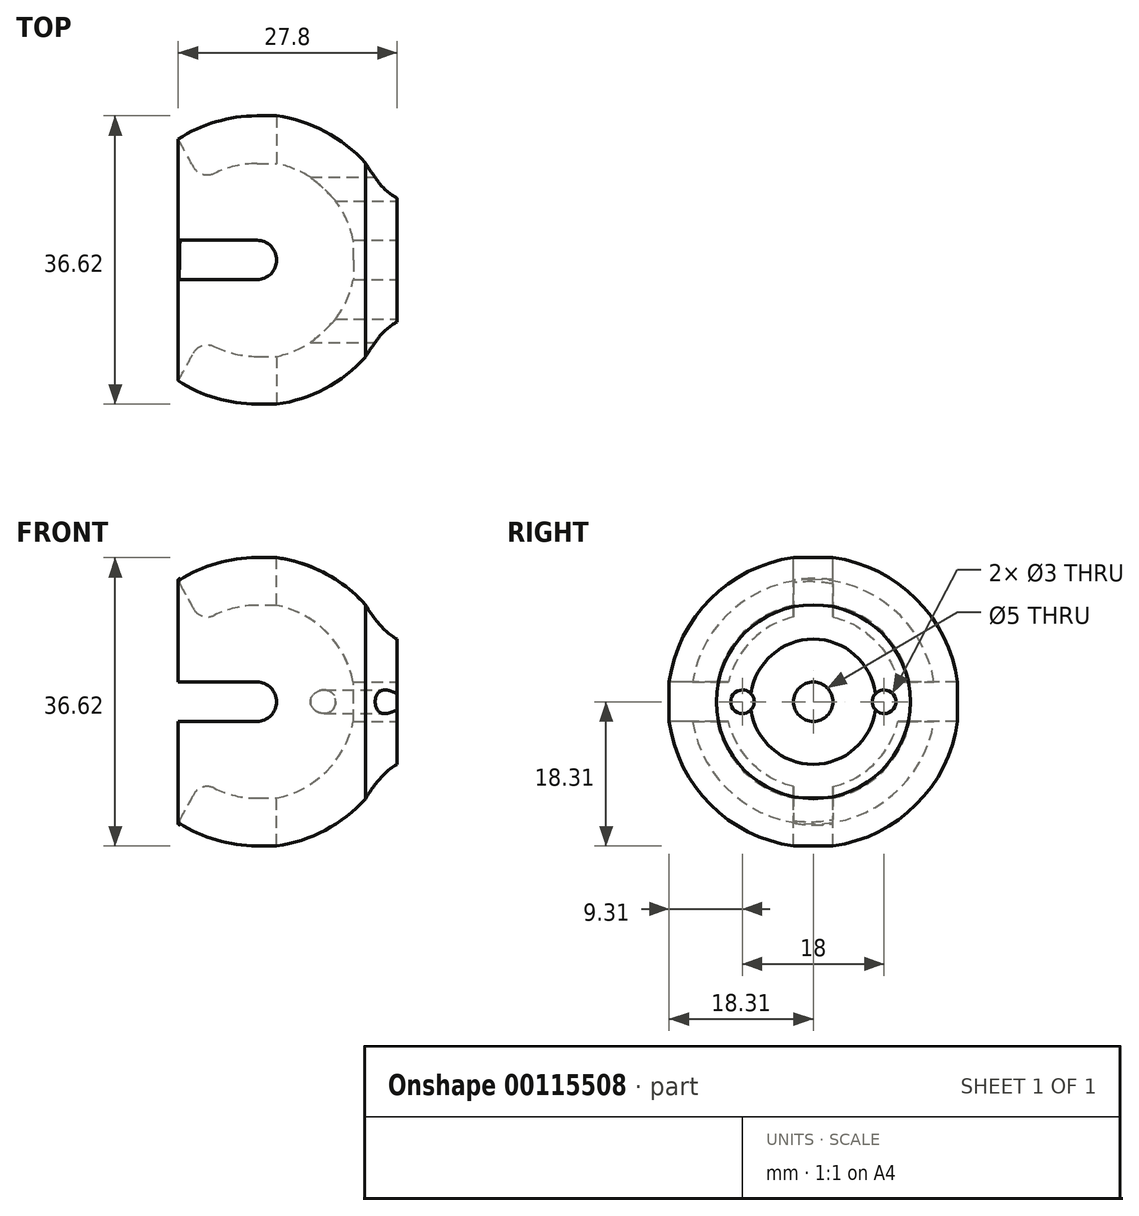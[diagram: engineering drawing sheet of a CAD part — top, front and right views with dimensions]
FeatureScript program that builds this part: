
annotation { "Feature Type Name" : "Feature", "Feature Type Description" : "" }
export const myFeature = defineFeature(function(context is Context, id is Id, definition is map)
    precondition{}
    {
        {
            var Q0;
            Q0=qCreatedBy(makeId("Front.planeOp"),FACE);
            var sketch = newSketch(context, id + "F0", { "sketchPlane" : qUnion([Q0])});
            skLineSegment(sketch, "E0", {"start": v(12.5, 0) * mm, "end": v(57.5, 0) * mm});
            skArc(sketch, "E1", {"start": v(12.46, 0.95) * mm, "mid": v(5.4, 11.27) * mm, "end": v(-7.07, 10.3) * mm});
            skFitSpline(sketch, "E2", {"points": [v(13.78, 12.32) * mm, v(24.8, 6.77) * mm, v(61.3, 8.08) * mm], "startDerivative": vector(27.08, -44.66) * mm, "endDerivative": vector(62.99, 8.12) * mm});
            skLineSegment(sketch, "E3", {"start": v(12.46, 0.95) * mm, "end": v(17.8, 0.95) * mm});
            skPoint(sketch, "E4.end.orphan", {"position": v(82.25, 0.95) * mm});
            skPoint(sketch, "E5.orphan", {"position": v(82.5, -1.55) * mm});
            skArc(sketch, "E6", {"start": v(13.78, 12.32) * mm, "mid": v(2.48, 18.32) * mm, "end": v(-10, 15.54) * mm});
            skLineSegment(sketch, "E7", {"start": v(-7.07, 10.3) * mm, "end": v(-10, 15.54) * mm});
            skLineSegment(sketch, "E8", {"start": v(17.8, 7.95) * mm, "end": v(17.8, 0.95) * mm});
            skPoint(sketch, "E9.start.orphan", {"position": v(74.25, 0.95) * mm});
            skSolve(sketch);
        }
        {
            var Q0;
            Q0=makeQuery(id+"F0.imprint","IMPRINT",FACE,{"disambiguationData":[TD([[makeQuery(id+"F0.imprint","IMPRINT",EDGE,{"derivedFrom":sQuery(id+"F0.wireOp",EDGE,"E1")}),-1.0]])]});
            var Q1;
            Q1=sQuery(id+"F0.wireOp",EDGE,"E0");
            revolve(context, id + "F1", {"entities" : qUnion([Q0]), "axis" : qUnion([Q1]), "revolveType" : RevolveType.FULL});
        }
        {
            var Q0;
            Q0=makeQuery(id+"F1.opRevolve","SWEPT_EDGE",EDGE,{"disambiguationData":[OSD([sQuery(id+"F0.wireOp",EDGE,"E1"),sQuery(id+"F0.wireOp",EDGE,"CbFEBDJi-CplH-pibZ-NPAv-z09MQRNn6UNR")])]});
            var Q1;
            Q1=makeQuery(id+"F1.opRevolve","SWEPT_EDGE",EDGE,{"disambiguationData":[OSD([sQuery(id+"F0.wireOp",EDGE,"E9"),sQuery(id+"F0.wireOp",EDGE,"8ef04d3b-c97b-4cb2-96d4-a3e5af4470d5.trimOffspring")])]});
            fillet(context, id + "F2", {"entities" : qUnion([Q0, Q1]), "radius" : 2 * mm, "tangentPropagation" : true, "allowEdgeOverflow" : false});
        }
        {
            var Q0;
            Q0=makeQuery(id+"F1.opRevolve","SWEPT_FACE",FACE,{"disambiguationData":[OSD([sQuery(id+"F0.wireOp",EDGE,"E8")])]});
            var sketch = newSketch(context, id + "F3", { "sketchPlane" : qUnion([Q0])});
            skCircle(sketch, "E10", {"center": v(-9, 0) * mm, "radius": 1.5 * mm});
            skCircle(sketch, "E11", {"center": v(9, 0) * mm, "radius": 1.5 * mm});
            skCircle(sketch, "E12", {"center": v(0, 0) * mm, "radius": 2.5 * mm});
            skSolve(sketch);
        }
        {
            var Q0;
            {var subQ0=sQuery(id+"F3.wireOp",EDGE,"E10");var subQ1=makeQuery(id+"F1.opRevolve","SWEPT_EDGE",EDGE,{"disambiguationData":[OSD([sQuery(id+"F0.wireOp",EDGE,"E2"),sQuery(id+"F0.wireOp",EDGE,"E8")])]});var subQ2=makeQuery(id+"F3.imprint","INTERSECT",VERTEX,{"disambiguationData":[OD(0.0)],"derivedFrom":[subQ1,subQ0]});Q0=makeQuery(id+"F3.imprint","IMPRINT",FACE,{"disambiguationData":[TD([[makeQuery(id+"F3.imprint","IMPRINT",EDGE,{"disambiguationData":[TD([[subQ2,-1.0]])],"derivedFrom":subQ0}),1.0]])]});}
            var Q1;
            {var subQ0=sQuery(id+"F3.wireOp",EDGE,"E11");var subQ1=makeQuery(id+"F1.opRevolve","SWEPT_EDGE",EDGE,{"disambiguationData":[OSD([sQuery(id+"F0.wireOp",EDGE,"E2"),sQuery(id+"F0.wireOp",EDGE,"E8")])]});var subQ2=makeQuery(id+"F3.imprint","INTERSECT",VERTEX,{"disambiguationData":[OD(0.0)],"derivedFrom":[subQ1,subQ0]});Q1=makeQuery(id+"F3.imprint","IMPRINT",FACE,{"disambiguationData":[TD([[makeQuery(id+"F3.imprint","IMPRINT",EDGE,{"disambiguationData":[TD([[subQ2,-1.0]])],"derivedFrom":subQ0}),1.0]])]});}
            var Q2;
            {var subQ0=sQuery(id+"F3.wireOp",EDGE,"E11");var subQ1=makeQuery(id+"F1.opRevolve","SWEPT_EDGE",EDGE,{"disambiguationData":[OSD([sQuery(id+"F0.wireOp",EDGE,"E2"),sQuery(id+"F0.wireOp",EDGE,"E8")])]});var subQ2=makeQuery(id+"F3.imprint","INTERSECT",VERTEX,{"disambiguationData":[OD(0.0)],"derivedFrom":[subQ1,subQ0]});Q2=makeQuery(id+"F3.imprint","IMPRINT",FACE,{"disambiguationData":[TD([[makeQuery(id+"F3.imprint","IMPRINT",EDGE,{"disambiguationData":[TD([[subQ2,1.0]])],"derivedFrom":subQ0}),1.0]])]});}
            var Q3;
            {var subQ0=sQuery(id+"F3.wireOp",EDGE,"E10");var subQ1=makeQuery(id+"F1.opRevolve","SWEPT_EDGE",EDGE,{"disambiguationData":[OSD([sQuery(id+"F0.wireOp",EDGE,"E2"),sQuery(id+"F0.wireOp",EDGE,"E8")])]});var subQ2=makeQuery(id+"F3.imprint","INTERSECT",VERTEX,{"disambiguationData":[OD(0.0)],"derivedFrom":[subQ1,subQ0]});Q3=makeQuery(id+"F3.imprint","IMPRINT",FACE,{"disambiguationData":[TD([[makeQuery(id+"F3.imprint","IMPRINT",EDGE,{"disambiguationData":[TD([[subQ2,1.0]])],"derivedFrom":subQ0}),1.0]])]});}
            extrude(context, id + "F4", {"entities" : qUnion([Q0, Q1, Q2, Q3]), "operationType" : NewBodyOperationType.REMOVE, "endBound" : BoundingType.THROUGH_ALL, "oppositeDirection" : true, "depth" : 25 * mm});
        }
        {
            var Q0;
            Q0=qSketchRegion(id+"F3",true);
            extrude(context, id + "F5", {"entities" : qUnion([Q0]), "operationType" : NewBodyOperationType.REMOVE, "endBound" : BoundingType.THROUGH_ALL, "oppositeDirection" : true, "depth" : 25 * mm});
        }
        {
            var Q0;
            Q0=qCreatedBy(makeId("Front.planeOp"),FACE);
            var sketch = newSketch(context, id + "F6", { "sketchPlane" : qUnion([Q0])});
            skArc(sketch, "E13", {"start": v(0, -2.5) * mm, "mid": v(2.5, 0) * mm, "end": v(0, 2.5) * mm});
            skLineSegment(sketch, "E14", {"start": v(0, 2.5) * mm, "end": v(-10.11, 2.5) * mm});
            skLineSegment(sketch, "E15", {"start": v(0, -2.5) * mm, "end": v(-10.11, -2.5) * mm});
            skLineSegment(sketch, "E16", {"start": v(-10.11, -2.5) * mm, "end": v(-10.11, 2.5) * mm});
            skSolve(sketch);
        }
        {
            var Q0;
            Q0 = qSketchRegion(id + "F6", true);
            extrude(context, id + "F7", {"entities" : qUnion([Q0]), "operationType" : NewBodyOperationType.REMOVE, "endBound" : BoundingType.SYMMETRIC, "oppositeDirection" : true, "depth" : 50 * mm});
        }
        {
            var Q0;
            Q0=qCreatedBy(makeId("Top.planeOp"),FACE);
            var sketch = newSketch(context, id + "F8", { "sketchPlane" : qUnion([Q0])});
            skArc(sketch, "E17", {"start": v(0, -2.5) * mm, "mid": v(2.5, 0) * mm, "end": v(0, 2.5) * mm});
            skLineSegment(sketch, "E18", {"start": v(0, 2.5) * mm, "end": v(-9.79, 2.5) * mm});
            skLineSegment(sketch, "E19", {"start": v(0, -2.5) * mm, "end": v(-9.88, -2.5) * mm});
            skLineSegment(sketch, "E20", {"start": v(-9.88, -2.5) * mm, "end": v(-9.79, 2.5) * mm});
            skSolve(sketch);
        }
        {
            var Q0;
            Q0 = qSketchRegion(id + "F8", true);
            extrude(context, id + "F9", {"entities" : qUnion([Q0]), "operationType" : NewBodyOperationType.REMOVE, "endBound" : BoundingType.SYMMETRIC, "oppositeDirection" : true, "depth" : 50 * mm});
        }
    });
